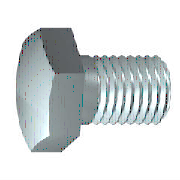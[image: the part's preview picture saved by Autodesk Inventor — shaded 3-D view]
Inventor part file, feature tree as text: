
AUTODESK INVENTOR PART (.ipt)
format: ipt  version: 2025.1 (Build 291241020, 241B)  size: 213,504 bytes
history: native  units: mm (DEFAULTED — no unit token found)
features: other x3, revolve x2, extrude x2, sketch x2, fillet x1
ambient origin geometry x8: Origin, YZ Plane, XZ Plane, XY Plane, X Axis, Y Axis, Z Axis, Center Point
bodies: Solid1 (feature_tree)
feature tree (10):
  revolve  "Revolution1"  Angle=45.0deg
  extrude  "Extrusion1"  TaperAngle=60.0deg  [1 undecoded]
  revolve  "Revolution2"  [1 undecoded]
  extrude  "Extrusion2"  TaperAngle=30.0deg  [1 undecoded]
  other  "MSC_A1"
  other  "MSC_PF1"
  other  "MSC_PT1"
  fillet  "Fillet1"  [1 undecoded]
  sketch  "Sketch2"  dims[d3=30.0deg d5=45.0deg]
  sketch  "Sketch4"  dims[d8=90.0deg d9=60.0deg d13=0.0mm d14=30.0deg d16=90.0deg d18=0.0mm d22=0.0mm d23=0.0mm d25=0.0mm d26=0.0mm d27=18.0mm d28=2.0mm d29=0.0mm d30=0.6mm d31=0.0mm]
note: 4 required parameter values undecoded (feature->parameter linkage not recoverable at this tier; creation-order binding heuristic only, values carry confidence <= 0.55)